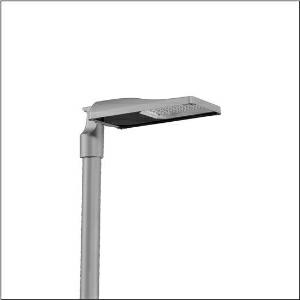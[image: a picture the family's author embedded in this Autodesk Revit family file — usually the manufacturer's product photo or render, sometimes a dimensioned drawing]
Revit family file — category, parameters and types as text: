
# Revit family: streetlight_sl_31_mini___st1_0a_5xh6d3aa08ga_9e06
name_source: partatom
category: Lighting Fixtures
units: mm (PartAtom-declared; Revit-internal decimal feet)

## family parameters
Cut with Voids When Loaded = No
Host = Face
Light Source = No
Part Type = Normal
Room Calculation Point = No
Round Connector Dimension = Use Diameter
Shared = No

## types (1)
- --- (1 x LED, 5710 lm, 37.3 W, 3000K)
    Apparent Load = 37 VA
    CIE Flux Codes = 37 72 97 100 100
    Color Rendering = 70
    Color Temperature = 3000K
    Default Elevation = 1800 mm
    Description = Streetlight SL 31 mini Easy mast luminaire for post-top, side-entry; light control with lens of PMMA; light distribution: ST1.0a, direct asymmetric distribution, for standard-compliant lighting for roads and squares; LED: luminous flux: 5.710lm, light colour: 730, colour temperature: 3000K; luminous efficacy: 153,1lm/W; control: pre-setting: linear dimming characteristic, flexible luminous flux parameterisation, time-dependent luminous flux control, constant luminous flux control, intelligent temperature release in ECG and LED module, overheat protection; luminaire housing, of diecast aluminium, SITECO metallic grey (DB 702S), corrosivity category C5 high according to DIN EN ISO 12944; cover of toughened safety glass, transparent, opened without tools; mast flange of diecast aluminium, SITECO metallic grey (DB 702S), spigot size: 76/60mm, mast flange included unmounted; cable length: 6,5m, connection cable pre-assembled; mains connection: 220..240V, AC, 50/60Hz; power consumption (at start of service life): 37,3W / (at end of service life): 38,7W / (with reduced operation 50%): 17,5W; protection rating (complete): IP66; insulation class (complete): insulation class II (safety insulation); impact resistance: IK10; certification: CE, ENEC, ENEC+, VDE, UKCA; permissible operating ambient temperature for outdoor applications: -40..+50°C; packaging unit: 1 piece

Light Distribution: ST1.0a
    Height = 76 mm
    Lamp = 1 x LED
    Lamp Light Flux = 5710 lm
    Lamp Power = 37.3 W
    Lamp count = 1
    Length = 547 mm
    Luminous efficacy = 153 lm/W
    Manufacturer = Siteco
    ModVariant = No
    Model = 5XH6D3AA08GA
    Number of Poles = 1
    OnlyDefault = Yes
    Power Factor = 1
    Product Name = Streetlight SL 31 mini | ST1.0a
    Product group = mast luminaire | pylon top
    ProductGroupID = 6100
    Protection Class = Protection class II
    Protection Degree = IP 66
    RLX_Detail_Level = 1
    RLX_Emergency_Light_Flux = 0 lm
    RLX_Emergency_Type = 0
    RLX_Emergency_Type_DB = No
    RlxData = <blob elided: 39649 chars, md5=607b7f06>
    Socket = socket
    Standby Power = 0 W
    System Light Flux = 5710 lm
    System Power = 37 W
    Type Comments = factory setting: luminous flux: 100 % | dim-lin: 254 | 386 mA
    Type Image = l_1300326.jpg
    URL = http://relux.com
    VarID = @adj_061057
    Voltage = 0 V
    Weight = 0.00 kg
    Width = 265 mm

## geometry (parser evidence)
native form markers: Blend x4, Sweep x11
no freeform markers — native parametric forms only
